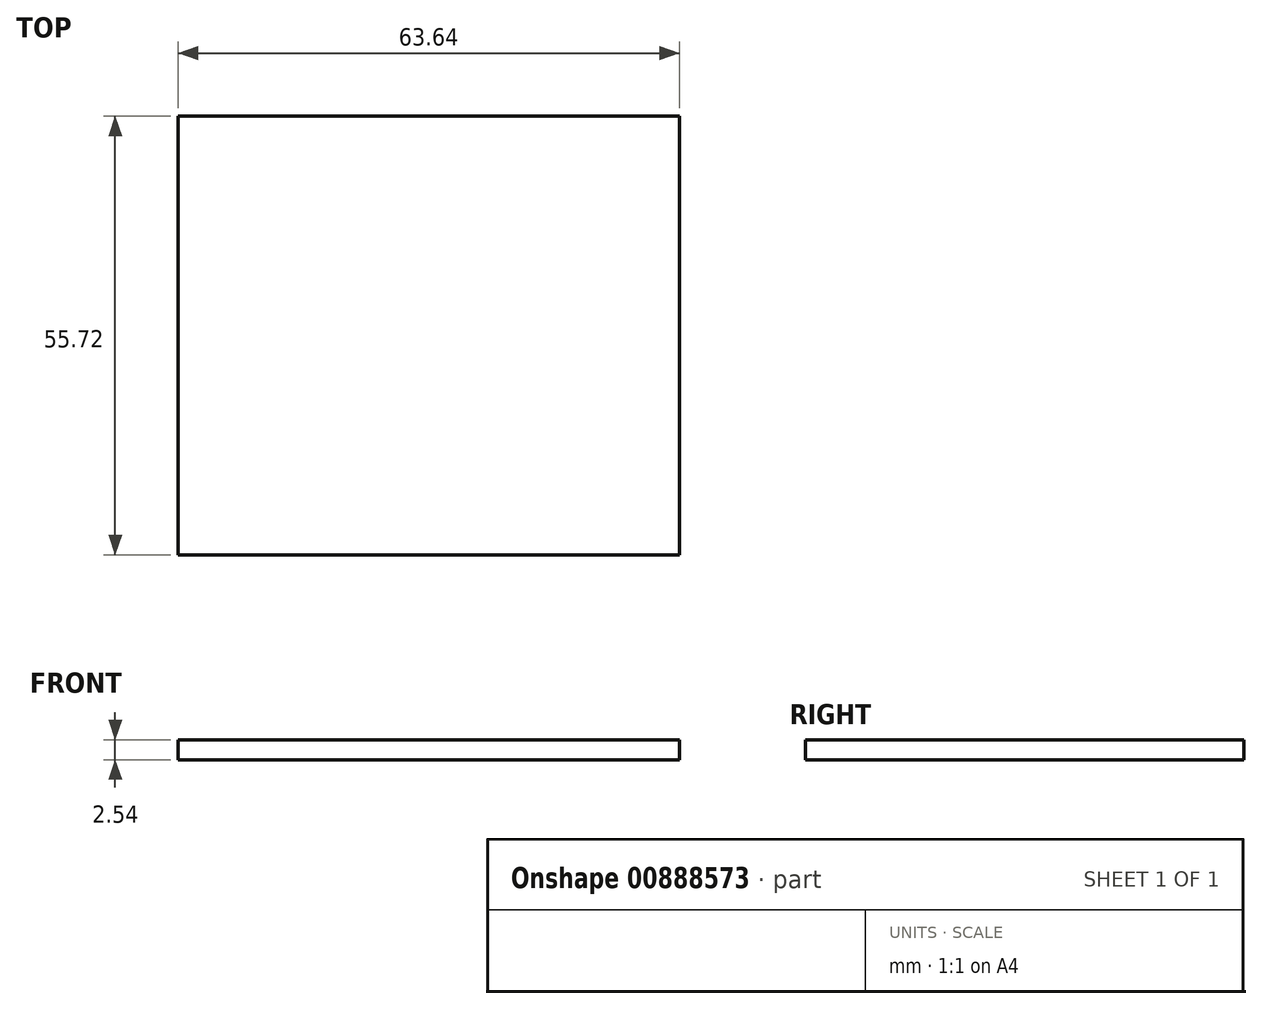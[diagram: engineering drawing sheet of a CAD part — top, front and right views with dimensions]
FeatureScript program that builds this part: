
annotation { "Feature Type Name" : "Feature", "Feature Type Description" : "" }
export const myFeature = defineFeature(function(context is Context, id is Id, definition is map)
    precondition{}
    {
        {
            var Q0;
            Q0=qCreatedBy(makeId("Top.planeOp"),FACE);
            var sketch = newSketch(context, id + "F0", { "sketchPlane" : qUnion([Q0])});
            skLineSegment(sketch, "E0.bottom", {"start": v(31.82, 27.86) * mm, "end": v(-31.82, 27.86) * mm});
            skLineSegment(sketch, "E0.top", {"start": v(31.82, -27.86) * mm, "end": v(-31.82, -27.86) * mm});
            skLineSegment(sketch, "E0.left", {"start": v(31.82, 27.86) * mm, "end": v(31.82, -27.86) * mm});
            skLineSegment(sketch, "E0.right", {"start": v(-31.82, 27.86) * mm, "end": v(-31.82, -27.86) * mm});
            skPoint(sketch, "E0.middle", {"position": v(0, 0) * mm});
            skSolve(sketch);
        }
        {
            var Q0;
            Q0 = qSketchRegion(id + "F0", true);
            extrude(context, id + "F1", {"entities" : qUnion([Q0]), "oppositeDirection" : true, "depth" : 2.54 * mm, "offsetDistance" : 25.4 * mm});
        }
    });
